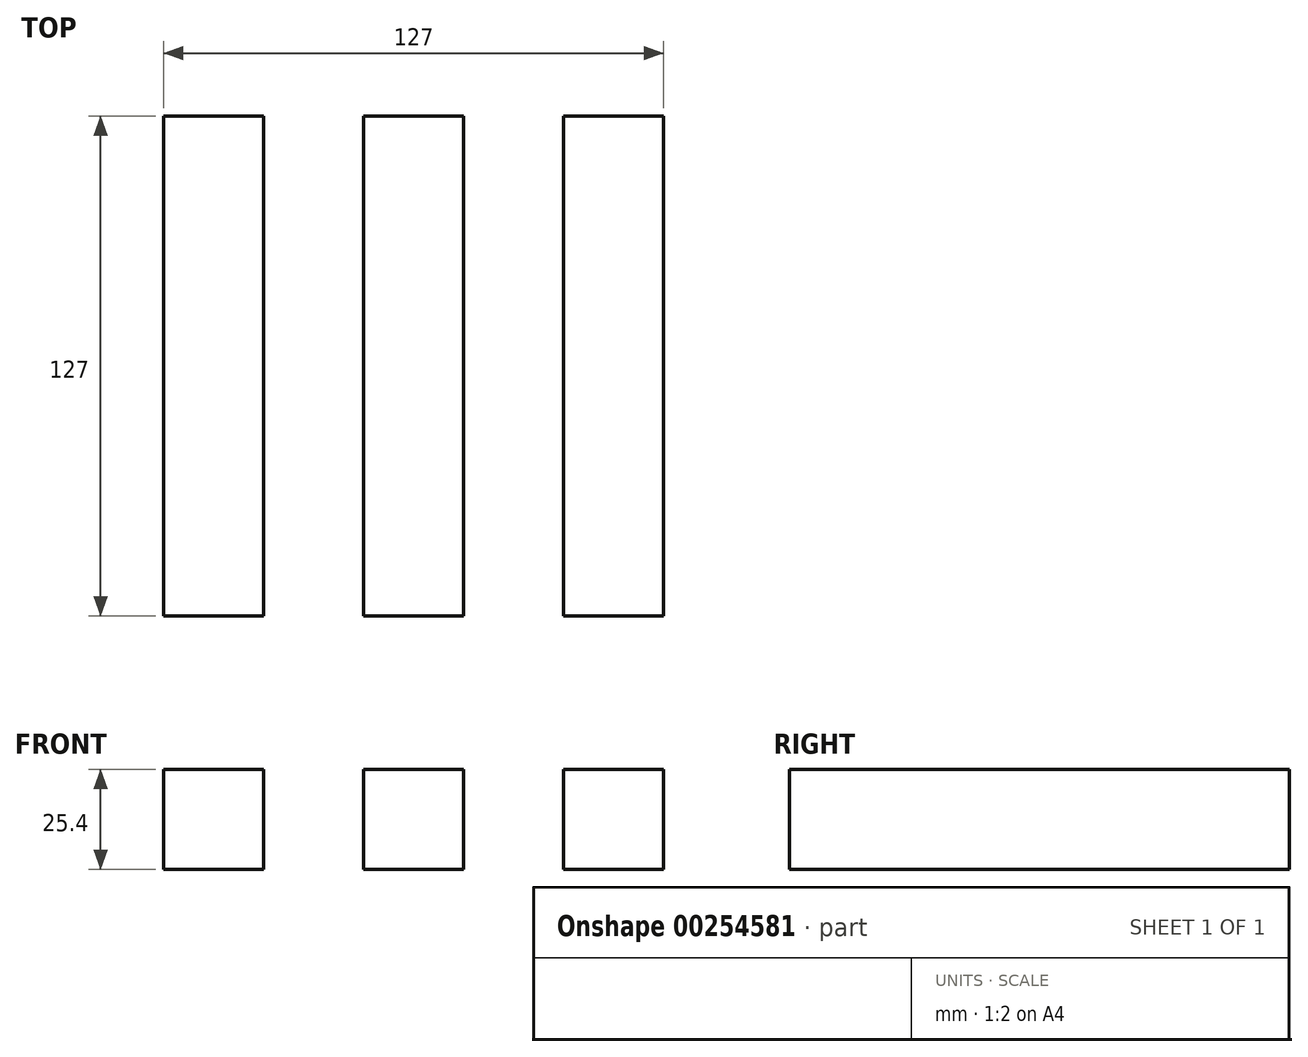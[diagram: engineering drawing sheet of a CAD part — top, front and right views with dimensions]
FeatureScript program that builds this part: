
annotation { "Feature Type Name" : "Feature", "Feature Type Description" : "" }
export const myFeature = defineFeature(function(context is Context, id is Id, definition is map)
    precondition{}
    {
        {
            var Q0;
            Q0=qCreatedBy(makeId("Front.planeOp"),FACE);
            var sketch = newSketch(context, id + "F0", { "sketchPlane" : qUnion([Q0])});
            skLineSegment(sketch, "E0.bottom", {"start": v(12.7, 12.7) * mm, "end": v(-12.7, 12.7) * mm});
            skLineSegment(sketch, "E0.top", {"start": v(12.7, -12.7) * mm, "end": v(-12.7, -12.7) * mm});
            skLineSegment(sketch, "E0.left", {"start": v(12.7, 12.7) * mm, "end": v(12.7, -12.7) * mm});
            skLineSegment(sketch, "E0.right", {"start": v(-12.7, 12.7) * mm, "end": v(-12.7, -12.7) * mm});
            skPoint(sketch, "E0.middle", {"position": v(0, 0) * mm});
            skLineSegment(sketch, "E1", {"start": v(0, 0) * mm, "end": v(50.8, 0) * mm});
            skLineSegment(sketch, "E2.bottom", {"start": v(63.5, 12.7) * mm, "end": v(38.1, 12.7) * mm});
            skLineSegment(sketch, "E2.top", {"start": v(63.5, -12.7) * mm, "end": v(38.1, -12.7) * mm});
            skLineSegment(sketch, "E2.left", {"start": v(63.5, 12.7) * mm, "end": v(63.5, -12.7) * mm});
            skLineSegment(sketch, "E2.right", {"start": v(38.1, 12.7) * mm, "end": v(38.1, -12.7) * mm});
            skPoint(sketch, "E2.middle", {"position": v(50.8, 0) * mm});
            skLineSegment(sketch, "E3", {"start": v(0, 0) * mm, "end": v(-50.8, 0) * mm});
            skLineSegment(sketch, "E4.bottom", {"start": v(-63.5, 12.7) * mm, "end": v(-38.1, 12.7) * mm});
            skLineSegment(sketch, "E4.top", {"start": v(-63.5, -12.7) * mm, "end": v(-38.1, -12.7) * mm});
            skLineSegment(sketch, "E4.left", {"start": v(-63.5, 12.7) * mm, "end": v(-63.5, -12.7) * mm});
            skLineSegment(sketch, "E4.right", {"start": v(-38.1, 12.7) * mm, "end": v(-38.1, -12.7) * mm});
            skPoint(sketch, "E4.middle", {"position": v(-50.8, 0) * mm});
            skSolve(sketch);
        }
        {
            var Q0;
            Q0 = qSketchRegion(id + "F0", true);
            extrude(context, id + "F1", {"entities" : qUnion([Q0]), "endBound" : BoundingType.SYMMETRIC, "depth" : 127 * mm});
        }
    });
